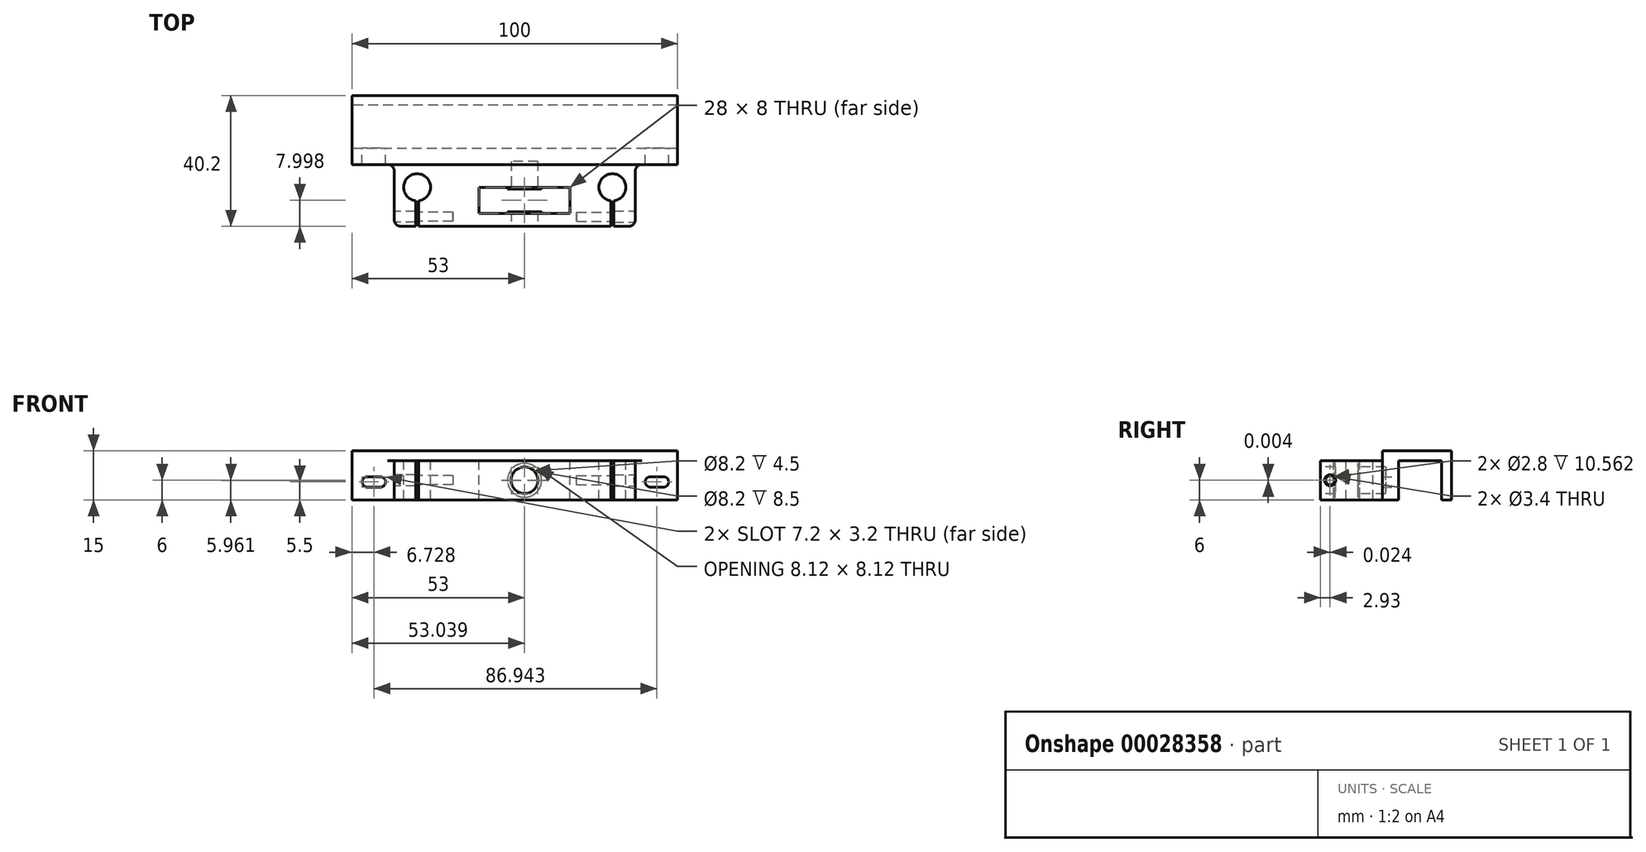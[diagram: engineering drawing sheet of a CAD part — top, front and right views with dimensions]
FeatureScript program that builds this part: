
annotation { "Feature Type Name" : "Feature", "Feature Type Description" : "" }
export const myFeature = defineFeature(function(context is Context, id is Id, definition is map)
    precondition{}
    {
        {
            var Q0;
            Q0=qCreatedBy(makeId("Top.planeOp"),FACE);
            var sketch = newSketch(context, id + "F0", { "sketchPlane" : qUnion([Q0])});
            skLineSegment(sketch, "E0", {"start": v(-46.35, 12.3) * mm, "end": v(53.65, 12.3) * mm});
            skLineSegment(sketch, "E1", {"start": v(53.65, 12.3) * mm, "end": v(53.65, 7.3) * mm});
            skLineSegment(sketch, "E2", {"start": v(53.65, 7.3) * mm, "end": v(40.65, 7.3) * mm});
            skLineSegment(sketch, "E3", {"start": v(40.65, 7.3) * mm, "end": v(40.65, -11.7) * mm});
            skLineSegment(sketch, "E4", {"start": v(40.65, -11.7) * mm, "end": v(-33.35, -11.7) * mm});
            skLineSegment(sketch, "E5", {"start": v(-33.35, -11.7) * mm, "end": v(-33.35, 7.3) * mm});
            skLineSegment(sketch, "E6", {"start": v(-33.35, 7.3) * mm, "end": v(-46.35, 7.3) * mm});
            skLineSegment(sketch, "E7", {"start": v(-46.35, 7.3) * mm, "end": v(-46.35, 12.3) * mm});
            skSolve(sketch);
        }
        {
            var Q0;
            Q0=qSketchRegion(id+"F0",true);
            extrude(context, id + "F1", {"entities" : qUnion([Q0]), "depth" : 12 * mm});
        }
        {
            var Q0;
            Q0=makeQuery(id+"F1.opExtrude","CAP_FACE",FACE,{"disambiguationData":[OSD([sQuery(id+"F0.wireOp",EDGE,"E0"),sQuery(id+"F0.wireOp",EDGE,"E1"),sQuery(id+"F0.wireOp",EDGE,"E2"),sQuery(id+"F0.wireOp",EDGE,"E3"),sQuery(id+"F0.wireOp",EDGE,"E4"),sQuery(id+"F0.wireOp",EDGE,"E5"),sQuery(id+"F0.wireOp",EDGE,"E6"),sQuery(id+"F0.wireOp",EDGE,"E7")])],"isStart":false});
            var sketch = newSketch(context, id + "F2", { "sketchPlane" : qUnion([Q0])});
            skCircle(sketch, "E8", {"center": v(-26.35, 0.3) * mm, "radius": 4.15 * mm});
            skCircle(sketch, "E9", {"center": v(33.65, 0.3) * mm, "radius": 4.15 * mm});
            skPoint(sketch, "E10", {"position": v(3.65, 12.3) * mm});
            skLineSegment(sketch, "E11.bottom", {"start": v(33.21, -3.01) * mm, "end": v(34.09, -3.01) * mm});
            skLineSegment(sketch, "E11.top", {"start": v(33.21, -12.27) * mm, "end": v(34.09, -12.27) * mm});
            skLineSegment(sketch, "E11.left", {"start": v(33.21, -3.01) * mm, "end": v(33.21, -12.27) * mm});
            skLineSegment(sketch, "E11.right", {"start": v(34.09, -3.01) * mm, "end": v(34.09, -12.27) * mm});
            skPoint(sketch, "E12", {"position": v(33.65, -3.01) * mm});
            skLineSegment(sketch, "E13", {"start": v(3.65, 12.3) * mm, "end": v(3.65, -11.7) * mm, "construction": true});
            skLineSegment(sketch, "E14.MirrorCS", {"start": v(-25.91, -12.27) * mm, "end": v(-26.79, -12.27) * mm});
            skLineSegment(sketch, "E15.MirrorCS", {"start": v(-26.79, -3.01) * mm, "end": v(-26.79, -12.27) * mm});
            skLineSegment(sketch, "E16.MirrorCS", {"start": v(-25.91, -3.01) * mm, "end": v(-26.79, -3.01) * mm});
            skLineSegment(sketch, "E17.MirrorCS", {"start": v(-25.91, -3.01) * mm, "end": v(-25.91, -12.27) * mm});
            skSolve(sketch);
        }
        {
            var Q0;
            Q0=qSketchRegion(id+"F2",true);
            var Q1;
            {var subQ3=sQuery(id+"F2.wireOp",EDGE,"E11.bottom");Q1=makeQuery(id+"F2.imprint","IMPRINT",FACE,{"disambiguationData":[TD([[makeQuery(id+"F2.imprint","IMPRINT",EDGE,{"derivedFrom":subQ3}),-1.0]])]});}
            var Q2;
            {var subQ3=sQuery(id+"F2.wireOp",EDGE,"E16.MirrorCS");Q2=makeQuery(id+"F2.imprint","IMPRINT",FACE,{"disambiguationData":[TD([[makeQuery(id+"F2.imprint","IMPRINT",EDGE,{"derivedFrom":subQ3}),1.0]])]});}
            extrude(context, id + "F3", {"entities" : qUnion([Q0, Q1, Q2]), "operationType" : NewBodyOperationType.REMOVE, "endBound" : BoundingType.THROUGH_ALL, "oppositeDirection" : true, "depth" : 25 * mm});
        }
        {
            var Q0;
            Q0=makeQuery(id+"F1.opExtrude","SWEPT_FACE",FACE,{"disambiguationData":[OSD([sQuery(id+"F0.wireOp",EDGE,"E0")])]});
            var sketch = newSketch(context, id + "F4", { "sketchPlane" : qUnion([Q0])});
            skLineSegment(sketch, "E18", {"start": v(-53.65, 5.5) * mm, "end": v(46.35, 5.5) * mm, "construction": true});
            skLineSegment(sketch, "E19.bottom", {"start": v(-49.32, 7.1) * mm, "end": v(-45.32, 7.1) * mm});
            skLineSegment(sketch, "E19.top", {"start": v(-49.32, 3.9) * mm, "end": v(-45.32, 3.9) * mm});
            skArc(sketch, "E20", {"start": v(-45.32, 3.9) * mm, "mid": v(-43.72, 5.5) * mm, "end": v(-45.32, 7.1) * mm});
            skArc(sketch, "E21", {"start": v(-49.32, 7.1) * mm, "mid": v(-50.92, 5.5) * mm, "end": v(-49.32, 3.9) * mm});
            skLineSegment(sketch, "E22.top", {"start": v(37.62, 3.9) * mm, "end": v(41.62, 3.9) * mm});
            skLineSegment(sketch, "E22.bottom", {"start": v(37.62, 7.1) * mm, "end": v(41.62, 7.1) * mm});
            skArc(sketch, "E23", {"start": v(37.62, 7.1) * mm, "mid": v(36.02, 5.5) * mm, "end": v(37.62, 3.9) * mm});
            skArc(sketch, "E24", {"start": v(41.62, 3.9) * mm, "mid": v(43.22, 5.5) * mm, "end": v(41.62, 7.1) * mm});
            skLineSegment(sketch, "E25", {"start": v(-53.65, 12) * mm, "end": v(-53.65, 5.5) * mm, "construction": true});
            skSolve(sketch);
        }
        {
            var Q0;
            Q0=qSketchRegion(id+"F4",true);
            extrude(context, id + "F5", {"entities" : qUnion([Q0]), "operationType" : NewBodyOperationType.REMOVE, "endBound" : BoundingType.THROUGH_ALL, "oppositeDirection" : true, "depth" : 25 * mm});
        }
        {
            var Q0;
            Q0=makeQuery(id+"F1.opExtrude","SWEPT_FACE",FACE,{"disambiguationData":[OSD([sQuery(id+"F0.wireOp",EDGE,"E4")])]});
            var sketch = newSketch(context, id + "F6", { "sketchPlane" : qUnion([Q0])});
            skLineSegment(sketch, "E26", {"start": v(-33.35, 6) * mm, "end": v(40.65, 6) * mm, "construction": true});
            skCircle(sketch, "E27", {"center": v(6.65, 6) * mm, "radius": 4.1 * mm});
            skSolve(sketch);
        }
        {
            var Q0;
            Q0=qSketchRegion(id+"F6",true);
            extrude(context, id + "F7", {"entities" : qUnion([Q0]), "operationType" : NewBodyOperationType.REMOVE, "oppositeDirection" : true, "depth" : 20 * mm});
        }
        {
            var Q0;
            Q0=makeQuery(id+"F1.opExtrude","CAP_FACE",FACE,{"disambiguationData":[OSD([sQuery(id+"F0.wireOp",EDGE,"E0"),sQuery(id+"F0.wireOp",EDGE,"E1"),sQuery(id+"F0.wireOp",EDGE,"E2"),sQuery(id+"F0.wireOp",EDGE,"E3"),sQuery(id+"F0.wireOp",EDGE,"E4"),sQuery(id+"F0.wireOp",EDGE,"E5"),sQuery(id+"F0.wireOp",EDGE,"E6"),sQuery(id+"F0.wireOp",EDGE,"E7")])],"isStart":false});
            var sketch = newSketch(context, id + "F8", { "sketchPlane" : qUnion([Q0])});
            skLineSegment(sketch, "E28.bottom", {"start": v(-7.35, 0.3) * mm, "end": v(20.65, 0.3) * mm});
            skLineSegment(sketch, "E28.top", {"start": v(-7.35, -7.7) * mm, "end": v(20.65, -7.7) * mm});
            skLineSegment(sketch, "E28.left", {"start": v(-7.35, 0.3) * mm, "end": v(-7.35, -7.7) * mm});
            skLineSegment(sketch, "E28.right", {"start": v(20.65, 0.3) * mm, "end": v(20.65, -7.7) * mm});
            skLineSegment(sketch, "E29", {"start": v(6.65, 12.3) * mm, "end": v(6.65, -11.7) * mm, "construction": true});
            skLineSegment(sketch, "E30", {"start": v(6.65, 0.3) * mm, "end": v(6.65, -7.7) * mm});
            skSolve(sketch);
        }
        {
            var Q0;
            Q0=qSketchRegion(id+"F8",true);
            extrude(context, id + "F9", {"entities" : qUnion([Q0]), "operationType" : NewBodyOperationType.REMOVE, "endBound" : BoundingType.THROUGH_ALL, "oppositeDirection" : true, "depth" : 25 * mm});
        }
        {
            var Q0;
            Q0=makeQuery(id+"F9.boolean.opBoolean","COPY",FACE,{"derivedFrom":makeQuery(id+"F9.opExtrude","SWEPT_FACE",FACE,{"disambiguationData":[OSD([sQuery(id+"F8.wireOp",EDGE,"E28.bottom")])]})});
            var sketch = newSketch(context, id + "F10", { "sketchPlane" : qUnion([Q0])});
            skCircle(sketch, "E31", {"center": v(6.65, 6) * mm, "radius": 5.2 * mm});
            skSolve(sketch);
        }
        {
            var Q0;
            Q0=makeQuery(id+"F10.imprint","IMPRINT",FACE,{"disambiguationData":[TD([[makeQuery(id+"F10.imprint","IMPRINT",EDGE,{"derivedFrom":sQuery(id+"F10.wireOp",EDGE,"E31")}),1.0]])]});
            extrude(context, id + "F11", {"entities" : qUnion([Q0]), "operationType" : NewBodyOperationType.ADD, "depth" : 0.5 * mm});
        }
        {
            var Q0;
            Q0=makeQuery(id+"F9.boolean.opBoolean","COPY",FACE,{"derivedFrom":makeQuery(id+"F9.opExtrude","SWEPT_FACE",FACE,{"disambiguationData":[OSD([sQuery(id+"F8.wireOp",EDGE,"E28.top")])]})});
            var sketch = newSketch(context, id + "F12", { "sketchPlane" : qUnion([Q0])});
            skCircle(sketch, "E32", {"center": v(-6.65, 6) * mm, "radius": 5.25 * mm});
            skSolve(sketch);
        }
        {
            var Q0;
            Q0=makeQuery(id+"F12.imprint","IMPRINT",FACE,{"disambiguationData":[TD([[makeQuery(id+"F12.imprint","IMPRINT",EDGE,{"derivedFrom":sQuery(id+"F12.wireOp",EDGE,"E32")}),1.0]])]});
            extrude(context, id + "F13", {"entities" : qUnion([Q0]), "operationType" : NewBodyOperationType.ADD, "depth" : 0.5 * mm});
        }
        {
            var Q0;
            Q0=makeQuery(id+"F1.opExtrude","SWEPT_FACE",FACE,{"disambiguationData":[OSD([sQuery(id+"F0.wireOp",EDGE,"E3")])]});
            var sketch = newSketch(context, id + "F14", { "sketchPlane" : qUnion([Q0])});
            skCircle(sketch, "E33", {"center": v(-8.74, 6) * mm, "radius": 1.7 * mm});
            skCircle(sketch, "E34", {"center": v(-8.74, 6) * mm, "radius": 1.4 * mm});
            skLineSegment(sketch, "E35", {"start": v(-11.7, 6) * mm, "end": v(-3.84, 6) * mm, "construction": true});
            skSolve(sketch);
        }
        {
            var Q0;
            Q0=makeQuery(id+"F14.imprint","IMPRINT",FACE,{"disambiguationData":[TD([[makeQuery(id+"F14.imprint","IMPRINT",EDGE,{"derivedFrom":sQuery(id+"F14.wireOp",EDGE,"E34")}),1.0]])]});
            extrude(context, id + "F15", {"entities" : qUnion([Q0]), "operationType" : NewBodyOperationType.REMOVE, "oppositeDirection" : true, "depth" : 18 * mm});
        }
        {
            var Q0;
            Q0=makeQuery(id+"F14.imprint","IMPRINT",FACE,{"disambiguationData":[TD([[makeQuery(id+"F14.imprint","IMPRINT",EDGE,{"derivedFrom":sQuery(id+"F14.wireOp",EDGE,"E34")}),1.0]])]});
            var Q1;
            Q1=makeQuery(id+"F14.imprint","IMPRINT",FACE,{"disambiguationData":[TD([[makeQuery(id+"F14.imprint","IMPRINT",EDGE,{"derivedFrom":sQuery(id+"F14.wireOp",EDGE,"E33")}),1.0]])]});
            extrude(context, id + "F16", {"entities" : qUnion([Q0, Q1]), "operationType" : NewBodyOperationType.REMOVE, "endBound" : BoundingType.UP_TO_NEXT, "oppositeDirection" : true, "depth" : 7 * mm});
        }
        {
            var Q0;
            Q0=makeQuery(id+"F1.opExtrude","SWEPT_EDGE",EDGE,{"disambiguationData":[OSD([sQuery(id+"F0.wireOp",EDGE,"E2"),sQuery(id+"F0.wireOp",EDGE,"E3")])]});
            fillet(context, id + "F17", {"entities" : qUnion([Q0]), "radius" : 2 * mm, "tangentPropagation" : true, "allowEdgeOverflow" : false});
        }
        {
            var Q0;
            Q0=makeQuery(id+"F1.opExtrude","SWEPT_FACE",FACE,{"disambiguationData":[OSD([sQuery(id+"F0.wireOp",EDGE,"E5")])]});
            var sketch = newSketch(context, id + "F18", { "sketchPlane" : qUnion([Q0])});
            skCircle(sketch, "E36", {"center": v(8.76, 6) * mm, "radius": 1.7 * mm});
            skCircle(sketch, "E37", {"center": v(8.76, 6) * mm, "radius": 1.4 * mm});
            skLineSegment(sketch, "E38", {"start": v(8.76, 0) * mm, "end": v(8.76, 12) * mm, "construction": true});
            skSolve(sketch);
        }
        {
            var Q0;
            Q0=makeQuery(id+"F18.imprint","IMPRINT",FACE,{"disambiguationData":[TD([[makeQuery(id+"F18.imprint","IMPRINT",EDGE,{"derivedFrom":sQuery(id+"F18.wireOp",EDGE,"E37")}),1.0]])]});
            extrude(context, id + "F19", {"entities" : qUnion([Q0]), "operationType" : NewBodyOperationType.REMOVE, "oppositeDirection" : true, "depth" : 18 * mm});
        }
        {
            var Q0;
            Q0=makeQuery(id+"F18.imprint","IMPRINT",FACE,{"disambiguationData":[TD([[makeQuery(id+"F18.imprint","IMPRINT",EDGE,{"derivedFrom":sQuery(id+"F18.wireOp",EDGE,"E37")}),1.0]])]});
            var Q1;
            Q1=makeQuery(id+"F18.imprint","IMPRINT",FACE,{"disambiguationData":[TD([[makeQuery(id+"F18.imprint","IMPRINT",EDGE,{"derivedFrom":sQuery(id+"F18.wireOp",EDGE,"E36")}),1.0]])]});
            extrude(context, id + "F20", {"entities" : qUnion([Q0, Q1]), "operationType" : NewBodyOperationType.REMOVE, "endBound" : BoundingType.UP_TO_NEXT, "oppositeDirection" : true, "depth" : 25 * mm});
        }
        {
            var Q0;
            Q0=makeQuery(id+"F1.opExtrude","SWEPT_EDGE",EDGE,{"disambiguationData":[OSD([sQuery(id+"F0.wireOp",EDGE,"E5"),sQuery(id+"F0.wireOp",EDGE,"E6")])]});
            var Q1;
            Q1=makeQuery(id+"F1.opExtrude","SWEPT_EDGE",EDGE,{"disambiguationData":[OSD([sQuery(id+"F0.wireOp",EDGE,"E4"),sQuery(id+"F0.wireOp",EDGE,"E5")])]});
            var Q2;
            Q2=makeQuery(id+"F1.opExtrude","SWEPT_EDGE",EDGE,{"disambiguationData":[OSD([sQuery(id+"F0.wireOp",EDGE,"E3"),sQuery(id+"F0.wireOp",EDGE,"E4")])]});
            fillet(context, id + "F21", {"entities" : qUnion([Q0, Q1, Q2]), "radius" : 2 * mm, "tangentPropagation" : true, "allowEdgeOverflow" : false});
        }
        {
            var Q0;
            Q0=makeQuery(id+"F1.opExtrude","SWEPT_FACE",FACE,{"disambiguationData":[OSD([sQuery(id+"F0.wireOp",EDGE,"E7")])]});
            var sketch = newSketch(context, id + "F22", { "sketchPlane" : qUnion([Q0])});
            skLineSegment(sketch, "E39", {"start": v(-12.3, 12) * mm, "end": v(-25.5, 12) * mm});
            skLineSegment(sketch, "E40", {"start": v(-25.5, 12) * mm, "end": v(-25.5, 0) * mm});
            skLineSegment(sketch, "E41", {"start": v(-25.5, 0) * mm, "end": v(-28.5, 0) * mm});
            skLineSegment(sketch, "E42", {"start": v(-28.5, 0) * mm, "end": v(-28.5, 15) * mm});
            skLineSegment(sketch, "E43", {"start": v(-28.5, 15) * mm, "end": v(-7.3, 15) * mm});
            skLineSegment(sketch, "E44", {"start": v(-7.3, 15) * mm, "end": v(-7.3, 12) * mm});
            skSolve(sketch);
        }
        {
            var Q0;
            Q0=makeQuery(id+"F22.imprint","IMPRINT",FACE,{"disambiguationData":[TD([[makeQuery(id+"F22.imprint","IMPRINT",EDGE,{"derivedFrom":sQuery(id+"F22.wireOp",EDGE,"E39")}),-1.0]])]});
            var Q1;
            Q1=makeQuery(id+"F1.opExtrude","SWEPT_FACE",FACE,{"disambiguationData":[OSD([sQuery(id+"F0.wireOp",EDGE,"E1")])]});
            extrude(context, id + "F23", {"entities" : qUnion([Q0]), "operationType" : NewBodyOperationType.ADD, "endBound" : BoundingType.UP_TO_SURFACE, "oppositeDirection" : true, "endBoundEntityFace" : qUnion([Q1]), "depth" : 25 * mm});
        }
    });
